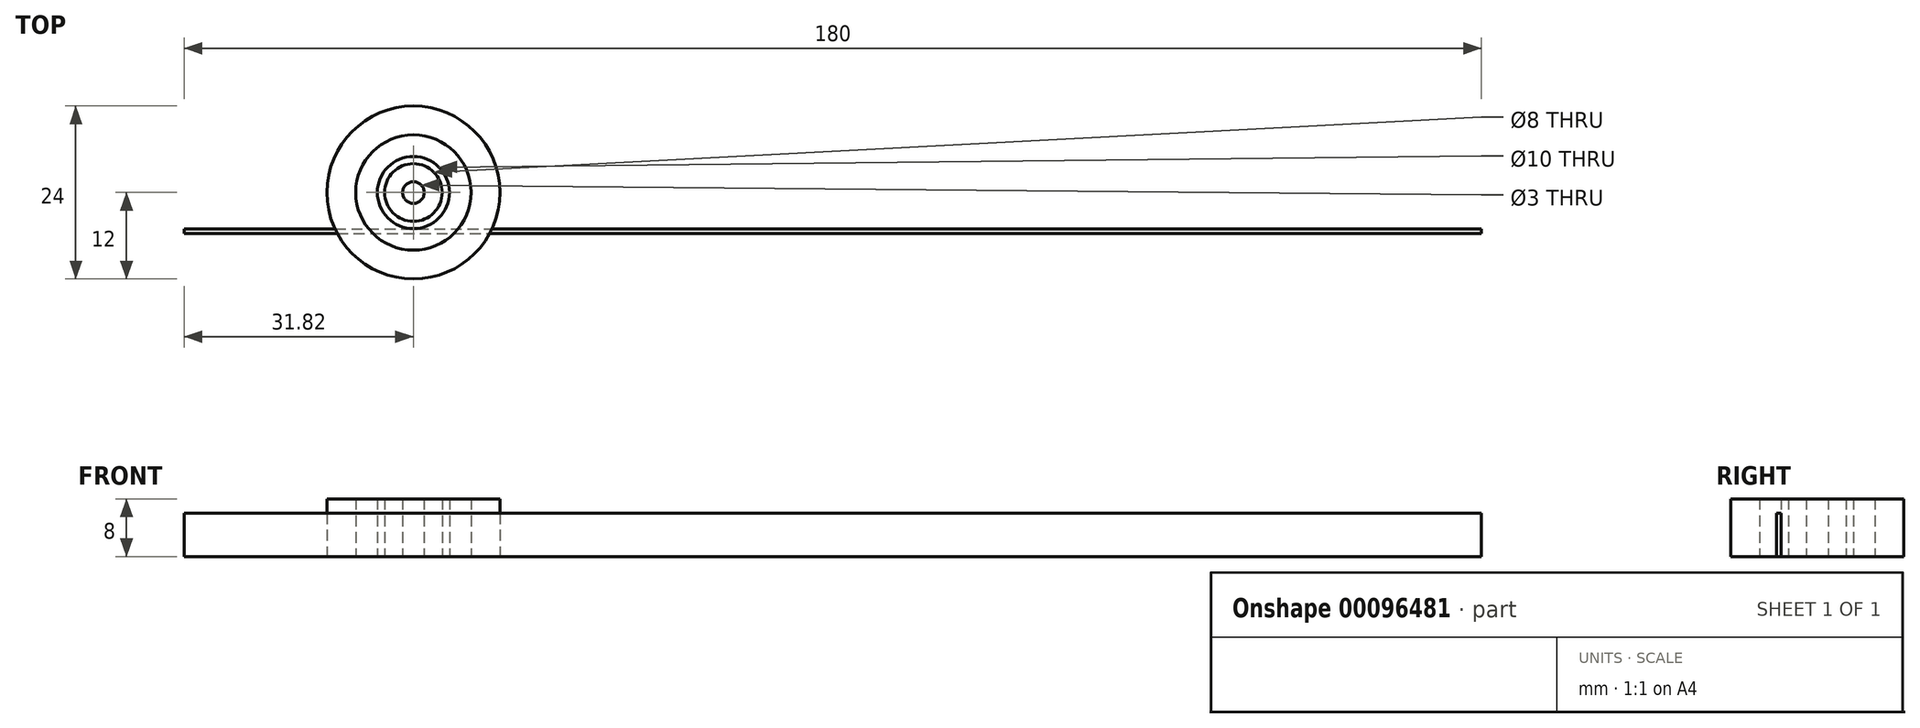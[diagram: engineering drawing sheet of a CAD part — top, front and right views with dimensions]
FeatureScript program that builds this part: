
annotation { "Feature Type Name" : "Feature", "Feature Type Description" : "" }
export const myFeature = defineFeature(function(context is Context, id is Id, definition is map)
    precondition{}
    {
        {
            var Q0;
            Q0=qCreatedBy(makeId("Top.planeOp"),FACE);
            var sketch = newSketch(context, id + "F0", { "sketchPlane" : qUnion([Q0])});
            skCircle(sketch, "E0", {"center": v(0, 0) * mm, "radius": 5 * mm});
            skCircle(sketch, "E1", {"center": v(0, 0) * mm, "radius": 1.5 * mm});
            skSolve(sketch);
        }
        {
            var Q0;
            Q0=makeQuery(id+"F0.imprint","IMPRINT",FACE,{"disambiguationData":[TD([[makeQuery(id+"F0.imprint","IMPRINT",EDGE,{"derivedFrom":sQuery(id+"F0.wireOp",EDGE,"E0")}),1.0]])]});
            extrude(context, id + "F1", {"entities" : qUnion([Q0]), "depth" : 8 * mm});
        }
        {
            var Q0;
            Q0=qCreatedBy(makeId("Top.planeOp"),FACE);
            var sketch = newSketch(context, id + "F2", { "sketchPlane" : qUnion([Q0])});
            skCircle(sketch, "E2", {"center": v(0, 0) * mm, "radius": 8 * mm});
            skCircle(sketch, "E3", {"center": v(0, 0) * mm, "radius": 5 * mm});
            skSolve(sketch);
        }
        {
            var Q0;
            Q0=qSketchRegion(id+"F2",true);
            extrude(context, id + "F3", {"entities" : qUnion([Q0]), "depth" : 8 * mm});
        }
        {
            var Q0;
            Q0=qCreatedBy(makeId("Top.planeOp"),FACE);
            var sketch = newSketch(context, id + "F4", { "sketchPlane" : qUnion([Q0])});
            skCircle(sketch, "E4", {"center": v(0, 0) * mm, "radius": 12 * mm});
            skCircle(sketch, "E5", {"center": v(0, 0) * mm, "radius": 4 * mm});
            skSolve(sketch);
        }
        {
            var Q0;
            Q0=makeQuery(id+"F4.imprint","IMPRINT",FACE,{"disambiguationData":[TD([[makeQuery(id+"F4.imprint","IMPRINT",EDGE,{"derivedFrom":sQuery(id+"F4.wireOp",EDGE,"E4")}),1.0]])]});
            extrude(context, id + "F5", {"entities" : qUnion([Q0]), "depth" : 8 * mm});
        }
        {
            var Q0;
            Q0=qCreatedBy(makeId("Top.planeOp"),FACE);
            var sketch = newSketch(context, id + "F6", { "sketchPlane" : qUnion([Q0])});
            skLineSegment(sketch, "E6.bottom", {"start": v(-31.82, -5.04) * mm, "end": v(148.18, -5.04) * mm});
            skLineSegment(sketch, "E6.top", {"start": v(-31.82, -5.67) * mm, "end": v(148.18, -5.67) * mm});
            skLineSegment(sketch, "E6.left", {"start": v(-31.82, -5.04) * mm, "end": v(-31.82, -5.67) * mm});
            skLineSegment(sketch, "E6.right", {"start": v(148.18, -5.04) * mm, "end": v(148.18, -5.67) * mm});
            skSolve(sketch);
        }
        {
            var Q0;
            Q0=qSketchRegion(id+"F6",true);
            extrude(context, id + "F7", {"entities" : qUnion([Q0]), "depth" : 6 * mm});
        }
    });
